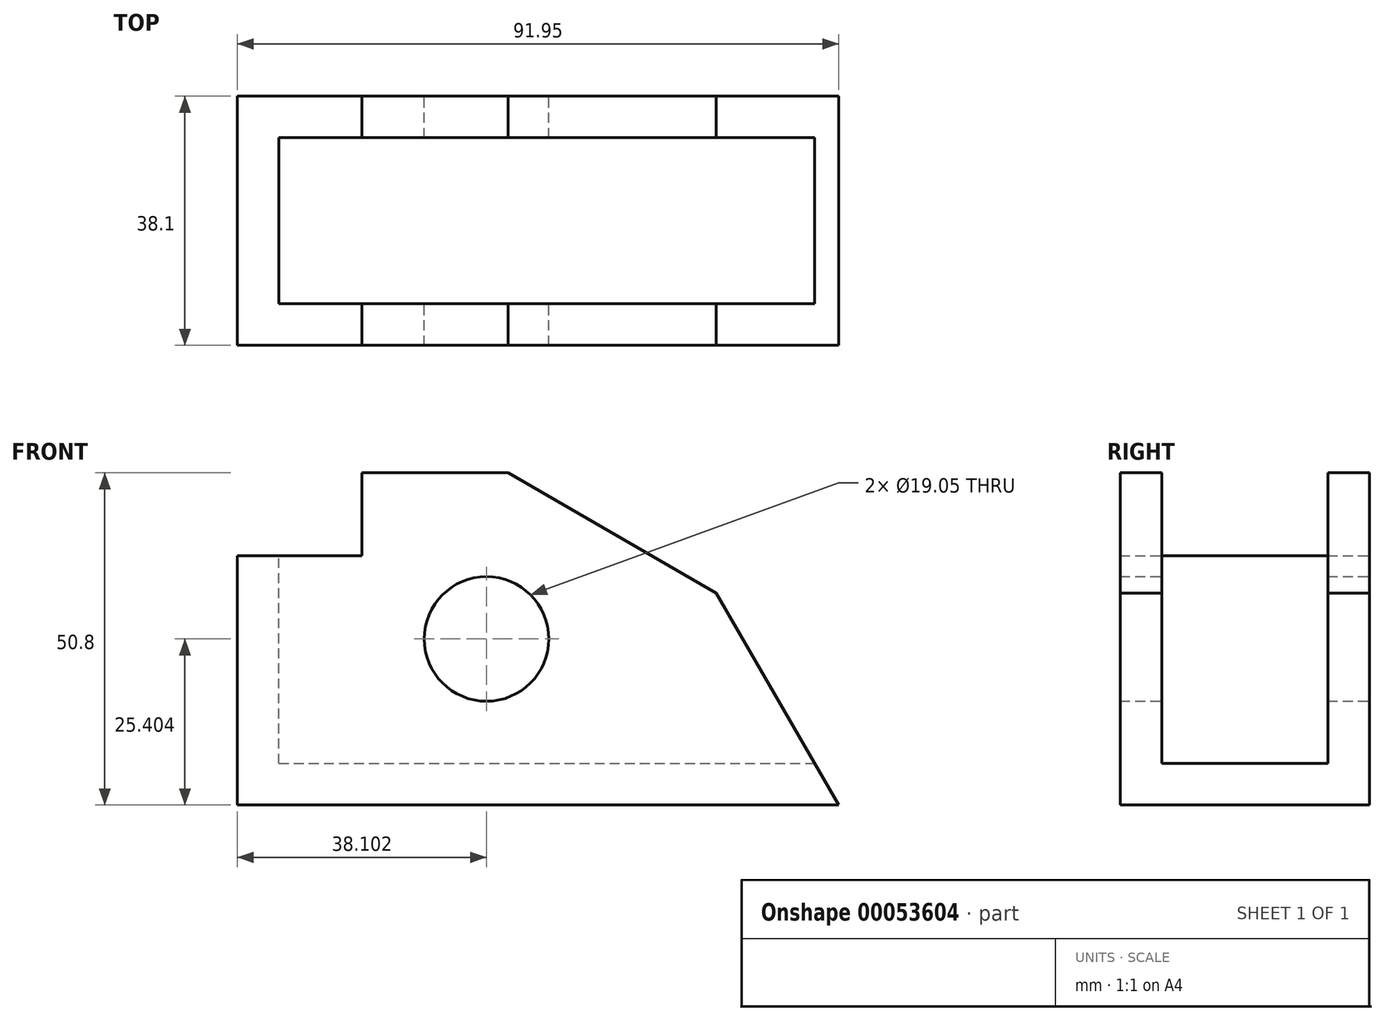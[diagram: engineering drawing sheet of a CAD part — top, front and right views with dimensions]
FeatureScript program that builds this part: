
annotation { "Feature Type Name" : "Feature", "Feature Type Description" : "" }
export const myFeature = defineFeature(function(context is Context, id is Id, definition is map)
    precondition{}
    {
        {
            var Q0;
            Q0=qCreatedBy(makeId("Front.planeOp"),FACE);
            var sketch = newSketch(context, id + "F0", { "sketchPlane" : qUnion([Q0])});
            skLineSegment(sketch, "E0", {"start": v(-415.18, 181.14) * mm, "end": v(-415.18, 143.04) * mm});
            skLineSegment(sketch, "E1", {"start": v(-415.18, 143.04) * mm, "end": v(-323.23, 143.04) * mm});
            skLineSegment(sketch, "E2", {"start": v(-323.23, 143.04) * mm, "end": v(-358.74, 204.54) * mm});
            skLineSegment(sketch, "E3", {"start": v(-415.18, 181.14) * mm, "end": v(-396.13, 181.14) * mm});
            skLineSegment(sketch, "E4", {"start": v(-396.13, 181.14) * mm, "end": v(-396.13, 193.84) * mm});
            skLineSegment(sketch, "E5", {"start": v(-396.13, 193.84) * mm, "end": v(-373.78, 193.84) * mm});
            skCircle(sketch, "E6", {"center": v(-377.08, 168.44) * mm, "radius": 9.53 * mm});
            skLineSegment(sketch, "E7", {"start": v(-373.78, 193.84) * mm, "end": v(-242.28, 117.92) * mm});
            skSolve(sketch);
        }
        {
            var Q0;
            Q0 = qSketchRegion(id + "F0", true);
            extrude(context, id + "F1", {"entities" : qUnion([Q0]), "depth" : 38.1 * mm});
        }
        {
            var Q0;
            Q0=makeQuery(id+"F1.opExtrude","SWEPT_FACE",FACE,{"disambiguationData":[OSD([sQuery(id+"F0.wireOp",EDGE,"E3")])]});
            var sketch = newSketch(context, id + "F2", { "sketchPlane" : qUnion([Q0])});
            skLineSegment(sketch, "E8.bottom", {"start": v(-408.83, -6.35) * mm, "end": v(-402.48, -6.35) * mm});
            skLineSegment(sketch, "E8.top", {"start": v(-408.83, -12.7) * mm, "end": v(-402.48, -12.7) * mm});
            skLineSegment(sketch, "E8.left", {"start": v(-408.83, -6.35) * mm, "end": v(-408.83, -12.7) * mm});
            skLineSegment(sketch, "E8.right", {"start": v(-402.48, -6.35) * mm, "end": v(-402.48, -12.7) * mm});
            skSolve(sketch);
        }
        {
            var Q0;
            Q0 = qSketchRegion(id + "F2", true);
            extrude(context, id + "F3", {"entities" : qUnion([Q0]), "operationType" : NewBodyOperationType.ADD, "depth" : 12.7 * mm});
        }
        {
            var Q0;
            Q0=makeQuery(id+"F3.opExtrude","CAP_FACE",FACE,{"disambiguationData":[OSD([sQuery(id+"F2.wireOp",EDGE,"E8.bottom"),sQuery(id+"F2.wireOp",EDGE,"E8.top"),sQuery(id+"F2.wireOp",EDGE,"E8.left"),sQuery(id+"F2.wireOp",EDGE,"E8.right")])],"isStart":false});
            var sketch = newSketch(context, id + "F4", { "sketchPlane" : qUnion([Q0])});
            skLineSegment(sketch, "E9.bottom", {"start": v(-408.83, -6.35) * mm, "end": v(-314.4, -6.35) * mm});
            skLineSegment(sketch, "E9.top", {"start": v(-408.83, -31.75) * mm, "end": v(-314.4, -31.75) * mm});
            skLineSegment(sketch, "E9.left", {"start": v(-408.83, -6.35) * mm, "end": v(-408.83, -31.75) * mm});
            skLineSegment(sketch, "E9.right", {"start": v(-314.4, -6.35) * mm, "end": v(-314.4, -31.75) * mm});
            skSolve(sketch);
        }
        {
            var Q0;
            Q0 = qSketchRegion(id + "F4", true);
            extrude(context, id + "F5", {"entities" : qUnion([Q0]), "operationType" : NewBodyOperationType.REMOVE, "oppositeDirection" : true, "depth" : 44.45 * mm});
        }
    });
